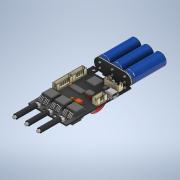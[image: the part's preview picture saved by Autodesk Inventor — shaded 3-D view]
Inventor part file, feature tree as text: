
AUTODESK INVENTOR PART (.ipt)
format: ipt  version: 2020.1 (Build 241239000, 239)  size: 2,895,360 bytes
history: native  units: mm
features: extrude x36, sketch x29, fillet x15, plane x11, pattern_linear x10, projected_geometry x7, sweep x5, chamfer x4, mirror x4, other x3, draft x2, revolve x2, pattern_circular x1
ambient origin geometry x8: Origin, YZ Plane, XZ Plane, XY Plane, X Axis, Y Axis, Z Axis, Center Point
bodies: Solid1 (feature_tree)
feature tree (129):
  sketch  "Sketch1"  dims[d0=38.0mm d1=65.0mm]
  extrude  "Extrusion1"  Depth=65.0mm
  extrude  "Extrusion4"  Depth=6.0mm
  extrude  "Extrusion5"  Depth=6.0mm
  extrude  "Extrusion6"  Depth=3.0mm
  extrude  "Extrusion7"  Depth=1.2mm TaperAngle=0.0deg
  extrude  "Extrusion8"  Depth=3.0mm
  extrude  "Extrusion10"  Depth=2.5mm
  extrude  "Extrusion12"  Depth=40.0mm
  extrude  "Extrusion13"  Depth=0.5mm
  extrude  "Extrusion14"  Depth=0.5mm
  extrude  "Extrusion15"  Depth=0.5mm
  extrude  "Extrusion16"  Depth=3.0mm
  extrude  "Extrusion17"  Depth=3.0mm
  extrude  "Extrusion18"  Depth=0.5mm
  extrude  "Extrusion19"  Depth=0.5mm
  extrude  "Extrusion20"  Depth=10.0mm
  extrude  "Extrusion21"  Depth=0.5mm
  fillet  "Fillet1"  Radius=1.8mm
  sketch  "Sketch6"  dims[d11=3.0mm d12=5.0mm]
  extrude  "Extrusion22"  Depth=5.5mm
  extrude  "Extrusion23"  Depth=2.0mm
  fillet  "Fillet2"  Radius=9.5mm
  fillet  "Fillet3"  Radius=9.5mm
  extrude  "Extrusion24"  Depth=3.0mm
  fillet  "Fillet4"  Radius=14.0mm
  extrude  "Extrusion25"  Depth=0.05mm
  chamfer  "Chamfer1"  Distance=0.5mm
  fillet  "Fillet5"  Radius=0.5mm
  chamfer  "Chamfer2"  Distance=1.8mm
  fillet  "Fillet6"  Radius=10.0mm
  draft  "FaceDraft1"
  plane  "Work Plane1"
  sketch  "Sketch10"  dims[d20=0.5mm d21=0.5mm]
  extrude  "Extrusion32"  Depth=0.05mm
  fillet  "Fillet14"  Radius=10.0mm
  pattern_linear  "Rectangular Pattern6"  Spacing1=10.0mm  [1 undecoded]
  sweep  "Sweep1"
  fillet  "Fillet7"  Radius=1.5mm
  plane  "Work Plane2"
  pattern_linear  "Rectangular Pattern1"  Spacing1=2.5mm  [1 undecoded]
  mirror  "Mirror1"
  pattern_linear  "Rectangular Pattern2"  Count1=3 Spacing1=12.0mm
  sketch  "Sketch11"  dims[d23=0.5mm d24=0.5mm d25=0.5mm d26=0.5mm]
  plane  "Work Plane3"
  sweep  "Sweep2"
  fillet  "Fillet8"  Radius=0.05mm
  pattern_linear  "Rectangular Pattern3"  Spacing1=6.0mm  [1 undecoded]
  plane  "Work Plane4"
  mirror  "Mirror2"
  sketch  "Sketch13"  dims[d29=3.0mm d30=3.0mm]
  extrude  "Extrusion26"  Depth=4.0mm
  extrude  "Extrusion27"  Depth=10.0mm
  draft  "FaceDraft2"
  fillet  "Fillet9"  Radius=2.0mm
  extrude  "Extrusion28"  Depth=0.05mm
  fillet  "Fillet10"  Radius=0.5mm
  extrude  "Extrusion29"  Depth=0.05mm
  fillet  "Fillet11"  Radius=7.0mm
  extrude  "Extrusion30"  Depth=2.0mm
  fillet  "Fillet12"  Radius=0.5mm
  extrude  "Extrusion31"  Depth=0.5mm
  mirror  "Mirror3"
  sketch  "Sketch16"  dims[d35=70.0mm d37=1.98mm d38=10.0mm d40=10.0mm d56=1.935mm]
  plane  "Work Plane5"
  sweep  "Sweep3"
  fillet  "Fillet13"  Radius=2.0mm
  pattern_linear  "Rectangular Pattern4"  Spacing1=2.0mm  [1 undecoded]
  plane  "Work Plane6"
  mirror  "Mirror4"
  pattern_linear  "Rectangular Pattern5"  Spacing1=1.0mm  [1 undecoded]
  extrude  "Extrusion33"  Depth=10.0mm
  fillet  "Fillet15"  Radius=5.0mm
  pattern_linear  "Rectangular Pattern7"  Spacing1=0.5mm  [1 undecoded]
  revolve  "Revolution1"  [1 undecoded]
  pattern_linear  "Rectangular Pattern8"  Spacing1=0.5mm  [1 undecoded]
  plane  "Work Plane11"
  extrude  "Extrusion35"  Depth=3.0mm
  revolve  "Revolution2"  [1 undecoded]
  extrude  "Extrusion36"  Depth=0.5mm
  chamfer  "Chamfer3"  Distance=0.5mm
  chamfer  "Chamfer4"  Distance=0.5mm
  pattern_linear  "Rectangular Pattern9"  Spacing1=0.5mm  [1 undecoded]
  plane  "Work Plane12"
  extrude  "Extrusion37"  Depth=0.05mm
  other  "Work Axis1"
  pattern_circular  "Circular Pattern1"  Count=4  [1 undecoded]
  pattern_linear  "Rectangular Pattern10"  Spacing1=1.78mm  [1 undecoded]
  sketch  "Sketch29"  dims[d80=2.0mm]
  plane  "Work Plane13"
  plane  "Work Plane14"
  sketch  "Sketch30"  dims[d81=0.5mm]
  sketch  "Sketch31"  dims[d82=3.0mm]
  sketch  "3D Sketch2"
  plane  "Work Plane15"
  sketch  "Sketch32"  dims[d83=3.0mm]
  sweep  "Sweep6"
  sweep  "Sweep7"
  extrude  "Extrusion38"  Depth=0.5mm
  extrude  "Extrusion39"  Depth=0.05mm
  extrude  "Extrusion40"  Depth=0.05mm
  extrude  "Extrusion41"  Depth=0.05mm
  sketch  "Sketch33"  dims[d84=0.5mm]
  sketch  "Sketch34"  dims[d85=0.5mm d86=0.5mm d87=0.5mm d88=1.8mm d89=60.0mm d91=1.98mm d92=10.0mm d94=10.0mm d96=1.8mm d97=10.0mm d98=10.0mm d99=2.0mm d100=1.5mm d101=2.5mm d102=30.0mm d104=12.0mm d105=10.0mm d107=10.0mm d109=2.0mm d110=0.05mm d111=6.0mm d112=4.0mm d113=30.0mm d115=12.0mm d116=10.0mm d118=10.0mm d120=2.0mm d121=11.0mm d122=0.5mm d123=1.0mm d124=8.0mm d125=7.0mm d126=2.0mm d127=0.5mm d128=0.5mm d129=0.5mm d130=2.0mm d131=2.0mm d132=1.0mm d133=10.0mm d134=5.0mm d135=0.5mm d136=0.5mm d137=0.5mm d138=3.0mm d139=3.0mm d140=0.5mm d141=0.5mm d142=0.5mm d143=0.5mm d144=1.78mm d145=40.0mm d147=1.98mm d148=10.0mm d150=10.0mm d152=1.78mm d153=7.5mm d154=0.5mm d155=0.5mm d156=3.75mm d157=3.75mm d158=6.0mm d159=3.75mm d160=3.75mm d161=3.75mm d162=3.75mm d164=5.0mm d165=4.5mm d178=1.5mm d179=1.5mm d180=3.0mm d185=1.5mm d186=1.5mm d188=1.5mm d189=1.0mm d190=1.5mm d191=0.5mm d192=3.0mm d193=4.0mm d194=1.0mm d195=3.0mm d206=0.5mm d207=0.05mm d208=1.8mm d209=1.0mm d210=0.0mm d211=1.5mm d212=0.0mm d213=2.0mm d214=0.0mm d215=3.0mm d216=0.0mm d217=5.0mm d218=0.0mm d221=5.0mm d222=0.0mm d225=6.0mm d226=0.0mm d227=1.0mm d228=0.0mm d229=3.0mm d230=0.0mm d231=4.0mm d232=0.0mm d233=4.5mm d234=0.0mm d235=1.0mm d236=1.0mm d237=1.0mm d238=1.0mm d239=1.0mm d240=1.0mm d241=2.0mm d242=0.0mm d243=0.3mm d244=0.3mm d245=0.3mm d246=0.3mm d247=1.5mm d248=0.0mm d249=0.05mm d250=0.5mm d251=0.5mm d252=0.5mm d253=2.0mm d254=0.0mm d255=0.5mm d256=0.5mm d257=0.5mm d258=2.0mm d259=0.0mm d260=0.5mm d261=0.5mm d262=0.5mm d263=2.0mm d264=0.0mm d265=0.5mm d266=0.3mm d267=1.0mm d268=1.0mm d269=6.5mm d270=0.0mm d271=0.7mm d272=0.7mm d273=0.0mm d274=0.3mm d275=0.5mm d276=45.0deg d277=135.0deg d279=1.5mm d280=4.5mm d281=1.0mm d282=5.5mm d283=0.0mm d284=0.2mm d285=0.7mm d286=0.5mm d287=0.5mm d288=3.5mm d289=0.55mm d290=0.55mm d291=7.0mm d292=0.0mm d293=0.2mm d294=2.0mm d295=45.0deg d296=0.5mm d297=0.2mm d298=2.0mm d299=45.0deg d300=2.0mm d301=1.22173mm d302=-0.5mm d311=2.0mm d312=0.4mm d313=0.0mm d314=0.0mm d315=1.0mm d316=3.0mm d317=2.0mm d318=1.0mm d319=3.0mm d320=1.0mm d321=0.5mm d322=30.0mm d324=1.34mm d325=30.0mm d327=12.0mm d328=0.1mm d329=0.1mm d330=0.5mm d331=0.1mm d332=-0.1mm d333=0.1mm d334=0.0mm d336=0.35mm d337=1.0mm d338=1.22173mm d339=0.0mm d340=0.0mm d341=0.5mm d342=280.0mm d344=0.47mm d345=10.0mm d346=10.0mm d348=12.0mm d349=1.5mm d350=2.0mm d351=2.0mm d352=2.0mm d353=2.0mm d354=10.0mm d355=7.0mm d356=7.0mm d357=7.0mm d358=6.0mm d359=8.5mm d360=6.0mm d361=5.0mm d362=0.2mm d363=2.0mm d364=4.0mm d365=6.0mm d366=1.0mm d367=1.0mm d368=0.0mm d369=4.5mm d370=0.0mm d371=1.22173mm d372=0.5mm d373=3.0mm d374=0.0mm d375=2.0mm d376=2.0mm d377=0.0mm d378=0.5mm d379=0.2mm d380=0.2mm d381=2.0mm d382=0.0mm d383=0.3mm d384=0.5mm d385=0.5mm d388=2.0mm d389=3.0mm d390=2.0mm d391=0.0mm d392=1.0mm d393=0.4mm d394=3.0mm d395=0.5mm d396=-0.5mm d397=2.0mm d398=1.0mm d399=3.0mm d400=2.0mm d401=0.0mm d402=0.0mm d403=1.0mm d404=30.0mm d406=1.34mm d407=30.0mm d409=12.0mm d410=1.0mm d411=2.0mm d412=0.0mm d413=1.0mm d414=30.0mm d416=12.0mm d417=1.0mm d418=2.0mm d419=0.0mm d420=1.0mm d421=30.0mm d423=12.0mm d424=2.25mm d425=20.0mm d426=1.0mm d427=30.543262mm d428=2.0mm d429=90.0deg d430=30.0mm d432=12.0mm d443=0.5mm d444=12.5mm d445=12.0mm d446=1.0mm d447=0.0mm d448=1.0mm d449=8.0mm d450=1.5mm d451=2.0mm d452=8.0mm d453=1.5mm d454=2.0mm d459=2.0mm d460=3.0mm d461=1.5mm d462=135.0deg d463=6.0mm d464=0.5mm d465=0.5mm d466=0.2mm d467=4.0mm d468=35.0mm d469=6.0mm d470=1.75mm d471=90.0deg d472=2.0mm d473=2.5mm d474=1.0mm d475=0.0mm d476=0.2mm d477=0.5mm d478=45.0deg d479=0.2mm d480=0.5mm d481=45.0deg d482=30.0mm d484=12.5mm d485=-0.1mm d488=0.3mm d489=30.0mm d491=360.0deg d493=5.0mm d494=0.0mm d495=30.0mm d496=360.0deg d498=30.0mm d500=12.5mm d501=2.0mm d502=2.25mm d504=4.5mm d506=2.48mm d507=0.0mm d508=0.0mm d509=0.0mm d510=0.0mm d511=40.0mm d512=0.0mm d513=38.0mm d514=0.0mm d518=2.5mm d519=1.0mm d520=0.8mm d522=0.0mm d523=2.0mm d524=30.0mm d526=1.5mm d527=10.0mm d529=10.0mm d531=0.05mm d532=0.0mm d533=0.05mm d534=0.0mm d536=1.24mm]
  sketch  "Sketch2"  dims[d2=6.0mm d3=6.0mm]
  projected_geometry  "Projected Loop1"
  projected_geometry  "Projected Loop2"
  projected_geometry  "Projected Loop3"
  sketch  "Sketch3"  dims[d4=6.0mm d5=6.0mm]
  sketch  "Sketch4"  dims[d6=3.0mm d7=3.5mm]
  sketch  "Sketch5"  dims[d8=3.0mm d9=1.2mm d10=0.0mm]
  sketch  "Sketch7"  dims[d13=2.5mm d14=24.0mm]
  sketch  "Sketch8"  dims[d15=54.05mm d16=40.0mm]
  sketch  "Sketch9"  dims[d18=4.5mm d19=0.5mm]
  sketch  "Sketch12"  dims[d27=3.0mm d28=3.0mm]
  projected_geometry  "Projected Loop4"
  sketch  "Sketch14"  dims[d31=0.5mm d32=0.5mm]
  projected_geometry  "Projected Loop5"
  sketch  "Sketch15"  dims[d33=0.5mm d34=1.935mm]
  sketch  "Sketch17"  dims[d58=0.5mm d59=0.5mm]
  projected_geometry  "Projected Loop6"
  sketch  "Sketch18"  dims[d61=60.0mm d63=1.98mm d64=10.0mm d66=10.0mm d68=1.8mm]
  sketch  "Sketch24"  dims[d69=13.0mm d70=5.5mm]
  sketch  "Sketch26"  dims[d71=2.0mm d72=7.5mm d73=9.5mm d74=9.5mm]
  sketch  "Sketch27"  dims[d75=3.0mm d76=6.0mm d77=14.0mm]
  projected_geometry  "Projected Loop14"
  sketch  "Sketch28"  dims[d78=0.05mm d79=5.0mm]
  other  "3D Intersection2"
  other  "3D Intersection3"
note: 12 required parameter values undecoded (feature->parameter linkage not recoverable at this tier; creation-order binding heuristic only, values carry confidence <= 0.55)